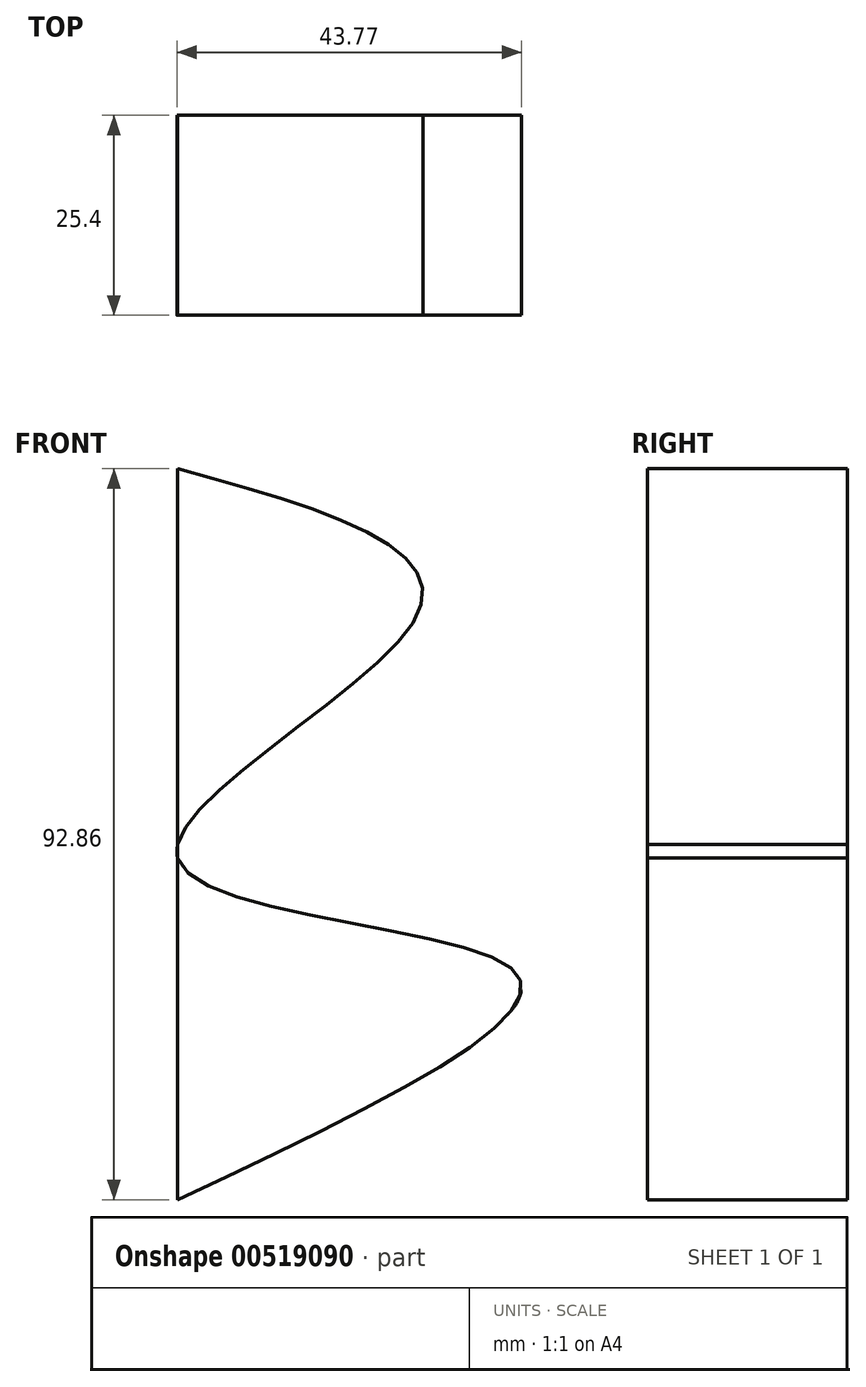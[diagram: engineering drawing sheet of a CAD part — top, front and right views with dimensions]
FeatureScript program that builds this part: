
annotation { "Feature Type Name" : "Feature", "Feature Type Description" : "" }
export const myFeature = defineFeature(function(context is Context, id is Id, definition is map)
    precondition{}
    {
        {
            var Q0;
            Q0=qCreatedBy(makeId("Front.planeOp"),FACE);
            var sketch = newSketch(context, id + "F0", { "sketchPlane" : qUnion([Q0])});
            skPoint(sketch, "E0.start.orphan", {"position": v(0, -43.4) * mm});
            skLineSegment(sketch, "E1", {"start": v(0, -43.4) * mm, "end": v(0, 49.45) * mm});
            skFitSpline(sketch, "E2", {"points": [v(0, 49.45) * mm, v(30.7, 31.47) * mm, v(0, 0) * mm, v(42.48, -14.1) * mm, v(0, -43.4) * mm], "startDerivative": vector(226.94, -62.58) * mm, "endDerivative": vector(-273.04, -128.48) * mm});
            skSolve(sketch);
        }
        {
            var Q0;
            Q0 = qSketchRegion(id + "F0", true);
            extrude(context, id + "F1", {"entities" : qUnion([Q0]), "depth" : 25.4 * mm});
        }
    });
